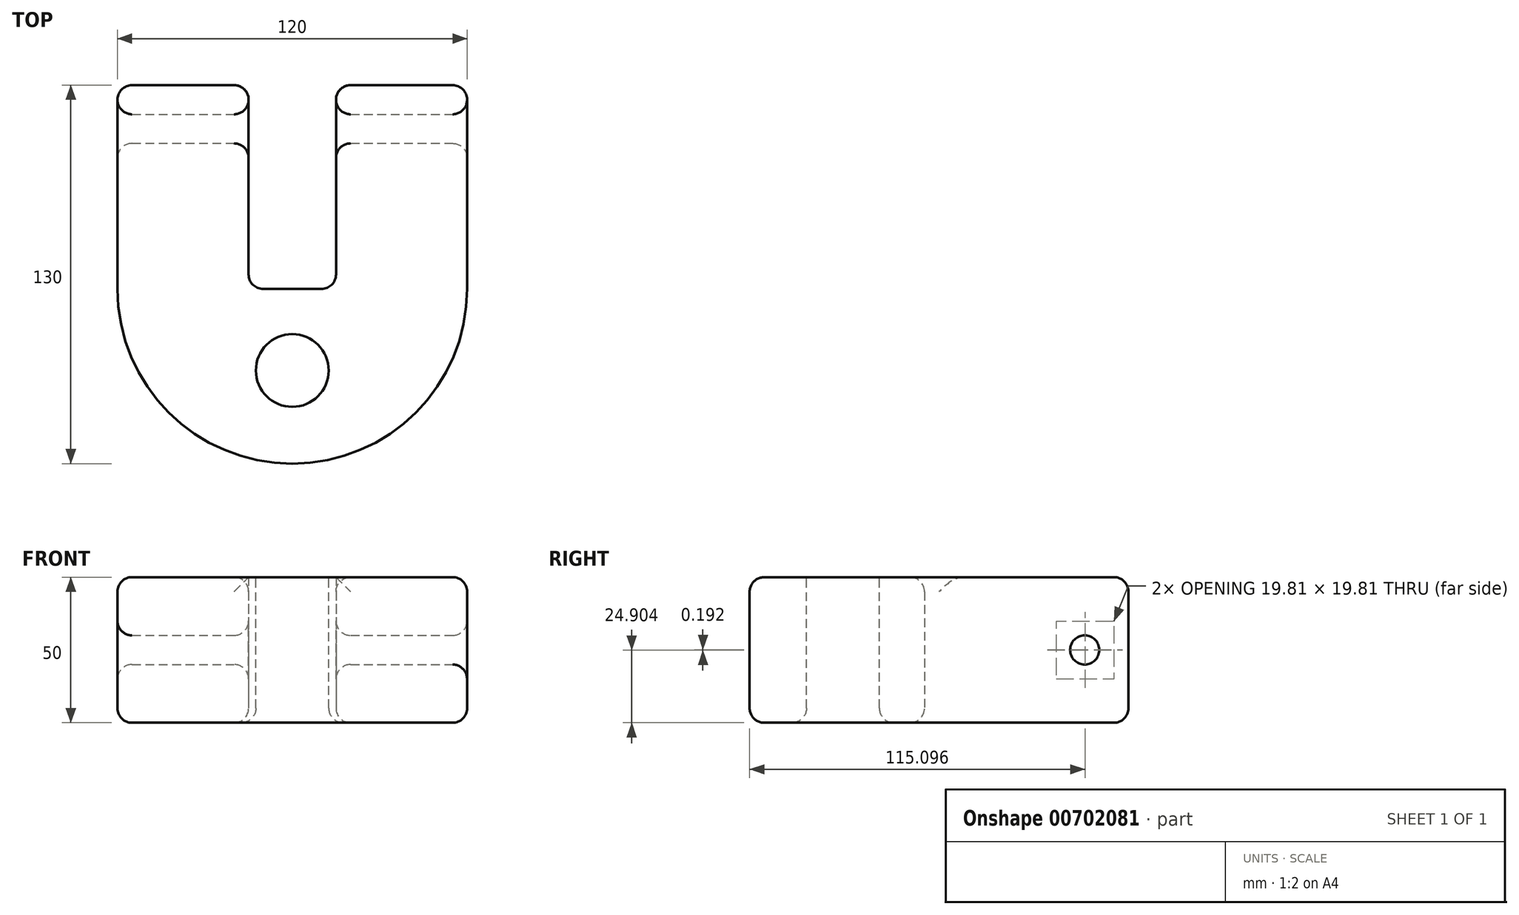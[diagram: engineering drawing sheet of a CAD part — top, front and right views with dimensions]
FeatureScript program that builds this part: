
annotation { "Feature Type Name" : "Feature", "Feature Type Description" : "" }
export const myFeature = defineFeature(function(context is Context, id is Id, definition is map)
    precondition{}
    {
        {
            var Q0;
            Q0=qCreatedBy(makeId("Top.planeOp"),FACE);
            var sketch = newSketch(context, id + "F0", { "sketchPlane" : qUnion([Q0])});
            skLineSegment(sketch, "E0", {"start": v(-60, 70) * mm, "end": v(-60, 0) * mm});
            skArc(sketch, "E1", {"start": v(-60, 0) * mm, "mid": v(0, -60) * mm, "end": v(60, 0) * mm});
            skLineSegment(sketch, "E2", {"start": v(60, 0) * mm, "end": v(60, 70) * mm});
            skLineSegment(sketch, "E3", {"start": v(-60, 70) * mm, "end": v(-15, 70) * mm});
            skLineSegment(sketch, "E4", {"start": v(-15, 70) * mm, "end": v(-15, 0) * mm});
            skLineSegment(sketch, "E5", {"start": v(-15, 0) * mm, "end": v(15, 0) * mm});
            skLineSegment(sketch, "E6", {"start": v(15, 0) * mm, "end": v(15, 70) * mm});
            skLineSegment(sketch, "E7", {"start": v(15, 70) * mm, "end": v(60, 70) * mm});
            skSolve(sketch);
        }
        {
            var Q0;
            Q0 = qSketchRegion(id + "F0", true);
            extrude(context, id + "F1", {"entities" : qUnion([Q0]), "depth" : 50 * mm, "offsetDistance" : 25 * mm});
        }
        {
            var Q0;
            Q0=makeQuery(id+"F1.opExtrude","CAP_FACE",FACE,{"disambiguationData":[OSD([sQuery(id+"F0.wireOp",EDGE,"E0"),sQuery(id+"F0.wireOp",EDGE,"E1"),sQuery(id+"F0.wireOp",EDGE,"E2"),sQuery(id+"F0.wireOp",EDGE,"E3"),sQuery(id+"F0.wireOp",EDGE,"E4"),sQuery(id+"F0.wireOp",EDGE,"E5"),sQuery(id+"F0.wireOp",EDGE,"E6"),sQuery(id+"F0.wireOp",EDGE,"E7")])],"isStart":false});
            var sketch = newSketch(context, id + "F2", { "sketchPlane" : qUnion([Q0])});
            skCircle(sketch, "E8", {"center": v(0, -28) * mm, "radius": 12.5 * mm});
            skSolve(sketch);
        }
        {
            var Q0;
            Q0 = qSketchRegion(id + "F2", true);
            extrude(context, id + "F3", {"entities" : qUnion([Q0]), "operationType" : NewBodyOperationType.REMOVE, "endBound" : BoundingType.THROUGH_ALL, "oppositeDirection" : true, "depth" : 25 * mm, "offsetDistance" : 25 * mm});
        }
        {
            var Q0;
            Q0=makeQuery(id+"F1.opExtrude","SWEPT_FACE",FACE,{"disambiguationData":[OSD([sQuery(id+"F0.wireOp",EDGE,"E2")])]});
            var sketch = newSketch(context, id + "F4", { "sketchPlane" : qUnion([Q0])});
            skCircle(sketch, "E9", {"center": v(55, 25) * mm, "radius": 5 * mm});
            skSolve(sketch);
        }
        {
            var Q0;
            Q0 = qSketchRegion(id + "F4", true);
            extrude(context, id + "F5", {"entities" : qUnion([Q0]), "operationType" : NewBodyOperationType.REMOVE, "endBound" : BoundingType.THROUGH_ALL, "oppositeDirection" : true, "depth" : 25 * mm, "offsetDistance" : 25 * mm});
        }
        {
            var Q0;
            Q0=makeQuery(id+"F3.boolean.opBoolean","COPY",EDGE,{"derivedFrom":makeQuery(id+"F3.opExtrude","CAP_EDGE",EDGE,{"disambiguationData":[OSD([sQuery(id+"F2.wireOp",EDGE,"E8")])],"isStart":true})});
            var Q1;
            Q1=makeQuery(id+"F1.opExtrude","CAP_EDGE",EDGE,{"disambiguationData":[OSD([sQuery(id+"F0.wireOp",EDGE,"E1")])],"isStart":false});
            var Q2;
            Q2=makeQuery(id+"F1.opExtrude","CAP_EDGE",EDGE,{"disambiguationData":[OSD([sQuery(id+"F0.wireOp",EDGE,"E5")])],"isStart":false});
            var Q3;
            Q3=makeQuery(id+"F1.opExtrude","SWEPT_FACE",FACE,{"disambiguationData":[OSD([sQuery(id+"F0.wireOp",EDGE,"E5")])]});
            var Q4;
            Q4=makeQuery(id+"F1.opExtrude","SWEPT_FACE",FACE,{"disambiguationData":[OSD([sQuery(id+"F0.wireOp",EDGE,"E7")])]});
            var Q5;
            Q5=makeQuery(id+"F1.opExtrude","SWEPT_FACE",FACE,{"disambiguationData":[OSD([sQuery(id+"F0.wireOp",EDGE,"E3")])]});
            var Q6;
            Q6=makeQuery(id+"F1.opExtrude","CAP_FACE",FACE,{"disambiguationData":[OSD([sQuery(id+"F0.wireOp",EDGE,"E0"),sQuery(id+"F0.wireOp",EDGE,"E1"),sQuery(id+"F0.wireOp",EDGE,"E2"),sQuery(id+"F0.wireOp",EDGE,"E3"),sQuery(id+"F0.wireOp",EDGE,"E4"),sQuery(id+"F0.wireOp",EDGE,"E5"),sQuery(id+"F0.wireOp",EDGE,"E6"),sQuery(id+"F0.wireOp",EDGE,"E7")])],"isStart":true});
            var Q7;
            Q7=makeQuery(id+"F5.boolean.opBoolean","COPY",FACE,{"disambiguationData":[TD([makeQuery(id+"F1.opExtrude","SWEPT_FACE",FACE,{"disambiguationData":[OSD([sQuery(id+"F0.wireOp",EDGE,"E0")])]})])],"derivedFrom":makeQuery(id+"F5.opExtrude","SWEPT_FACE",FACE,{"disambiguationData":[OSD([sQuery(id+"F4.wireOp",EDGE,"E9")])]})});
            var Q8;
            Q8=makeQuery(id+"F5.boolean.opBoolean","COPY",FACE,{"disambiguationData":[TD([makeQuery(id+"F1.opExtrude","SWEPT_FACE",FACE,{"disambiguationData":[OSD([sQuery(id+"F0.wireOp",EDGE,"E2")])]})])],"derivedFrom":makeQuery(id+"F5.opExtrude","SWEPT_FACE",FACE,{"disambiguationData":[OSD([sQuery(id+"F4.wireOp",EDGE,"E9")])]})});
            fillet(context, id + "F6", {"entities" : qUnion([Q0, Q1, Q2, Q3, Q4, Q5, Q6, Q7, Q8]), "radius" : 5 * mm, "tangentPropagation" : true, "allowEdgeOverflow" : false});
        }
    });
